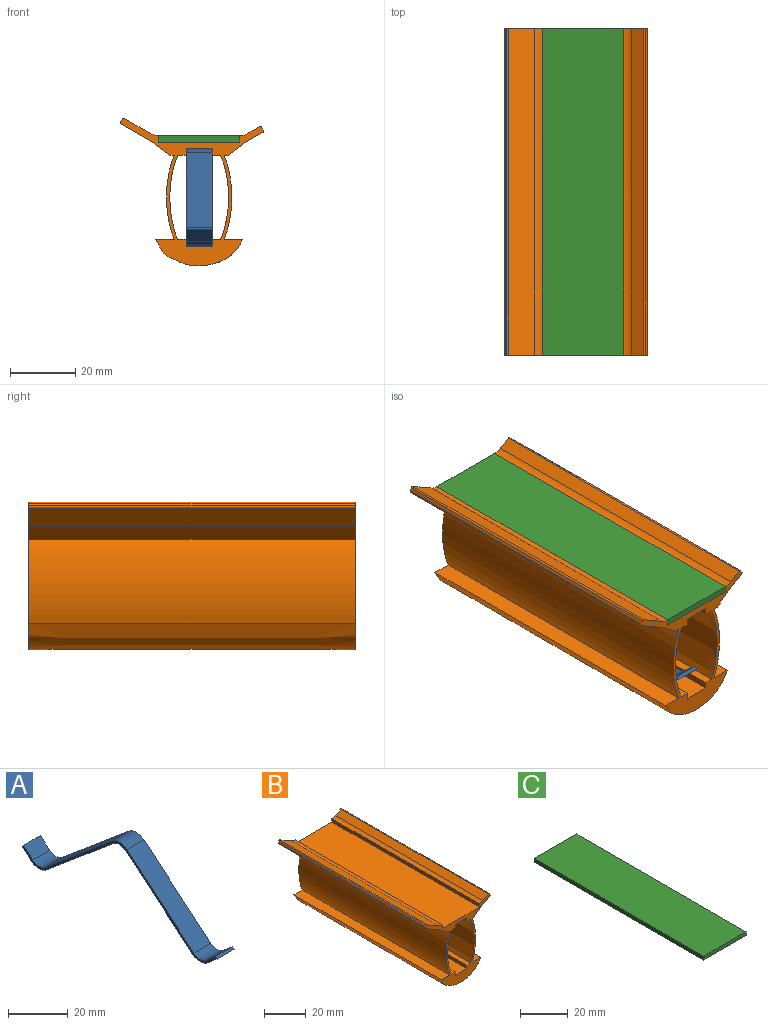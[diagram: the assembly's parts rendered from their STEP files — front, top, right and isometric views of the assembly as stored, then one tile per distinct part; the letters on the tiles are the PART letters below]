
ASSEMBLY  parts=3 mates=2
PART A: 18 faces, bbox 8x91.9x29.8 mm
  f0: plane 8x4.45mm, normal (0,0.64,0.77), area 46.4mm2, adj f1,f15,f16,f17
  f1: plane 8x0.77mm, normal (0,-0.77,0.64), area 8mm2, adj f0,f2,f16,f17
  f2: plane 8x4.45mm, normal (0,-0.64,-0.77), area 46.4mm2, adj f1,f3,f16,f17
  f3: cylinder r=5.5mm len=8mm, axis (-1,0,0), area 61.4mm2, adj f2,f4,f16,f17
  f4: plane 31.56x26.48mm, normal (0,0.64,-0.77), area 329.6mm2, adj f3,f5,f16,f17
  f5: cylinder r=4.5mm len=8mm, axis (-1,0,0), area 50.3mm2, adj f4,f6,f16,f17
  f6: plane 31.56x26.48mm, normal (0,-0.64,-0.77), area 329.6mm2, adj f5,f7,f16,f17
  f7: cylinder r=5.5mm len=8mm, axis (-1,0,0), area 61.4mm2, adj f6,f8,f16,f17
  f8: plane 8x4.45mm, normal (0,0.64,-0.77), area 46.4mm2, adj f7,f9,f16,f17
  f9: plane 8x0.77mm, normal (0,0.77,0.64), area 8mm2, adj f8,f10,f16,f17
  f10: plane 8x4.45mm, normal (0,-0.64,0.77), area 46.4mm2, adj f9,f11,f16,f17
  f11: cylinder r=4.5mm len=8mm, axis (-1,0,0), area 50.3mm2, adj f10,f12,f16,f17
  f12: plane 31.56x26.48mm, normal (0,0.64,0.77), area 329.6mm2, adj f11,f13,f16,f17
  f13: cylinder r=5.5mm len=8mm, axis (-1,0,0), area 61.4mm2, adj f12,f14,f16,f17
  f14: plane 31.56x26.48mm, normal (0,-0.64,0.77), area 329.6mm2, adj f13,f15,f16,f17
  f15: cylinder r=4.5mm len=8mm, axis (-1,0,0), area 50.3mm2, adj f0,f14,f16,f17
  f16: plane 91.95x29.82mm, normal (1,0,0), area 115mm2, adj f0,f1,f2,f3,f4,f5,f6,f7
  f17: plane 91.95x29.82mm, normal (-1,0,0), area 115mm2, adj f0,f1,f2,f3,f4,f5,f6,f7
PART B: 38 faces, bbox 43.9x100x45.3 mm
  f0: plane 45.29x43.89mm, normal (0,-1,0), area 313.5mm2, adj f1,f2,f3,f4,f5,f6,f7,f8
  f1: cylinder r=5mm len=100mm, axis (0,-1,0), area 252.8mm2, adj f0,f8,f10,f35
  f2: plane 100x2.55mm, normal (0,0,-1), area 254.7mm2, adj f0,f10,f15,f16
  f3: plane 100x1.36mm, normal (0,0,-1), area 136.3mm2, adj f0,f10,f20,f33
  f4: plane 100x9.58mm, normal (-0.5,0,-0.87), area 1106.1mm2, adj f0,f10,f31,f33
  f5: plane 100x5.23mm, normal (0.5,0,-0.87), area 603.6mm2, adj f0,f10,f28,f34
  f6: plane 100x0.87mm, normal (0.87,0,0.5), area 100mm2, adj f0,f10,f28,f29
  f7: plane 100x3.6mm, normal (-0.5,0,0.87), area 416mm2, adj f0,f10,f29,f32
  f8: plane 100x7.96mm, normal (0.5,0,0.87), area 918.6mm2, adj f0,f1,f10,f30
  f9: plane 100x0.87mm, normal (-0.87,0,0.5), area 100mm2, adj f0,f10,f30,f31
  f10: plane 45.29x43.89mm, normal (0,1,0), area 313.5mm2, adj f1,f2,f3,f4,f5,f6,f7,f8
  f11: plane 100x1.36mm, normal (0,0,-1), area 136.3mm2, adj f0,f10,f17,f34
  f12: plane 100x2.55mm, normal (0,0,-1), area 254.7mm2, adj f0,f10,f13,f19
  f13: plane 100x2mm, normal (1,0,0), area 200mm2, adj f0,f10,f12,f14
  f14: plane 100x8mm, normal (0,0,-1), area 800mm2, adj f0,f10,f13,f15
  f15: plane 100x2mm, normal (-1,0,0), area 200mm2, adj f0,f2,f10,f14
  f16: extruded ~100x25.82mm, area 2647.1mm2, adj f0,f2,f10,f18
  f17: extruded ~100x25.82mm, area 2642.1mm2, adj f0,f10,f11,f22
  f18: plane 100x2.55mm, normal (0,0,1), area 254.7mm2, adj f0,f10,f16,f27
  f19: extruded ~100x25.82mm, area 2647.1mm2, adj f0,f10,f12,f23
  f20: extruded ~100x25.82mm, area 2642.1mm2, adj f0,f3,f10,f21
  f21: plane 100x5.68mm, normal (0,0,1), area 567.6mm2, adj f0,f10,f20,f24
  f22: plane 100x5.63mm, normal (0,0,1), area 563.3mm2, adj f0,f10,f17,f24
  f23: plane 100x2.55mm, normal (0,0,1), area 254.7mm2, adj f0,f10,f19,f26
  f24: extruded ~100x26.58mm, area 3317.3mm2, adj f0,f10,f21,f22
  f25: plane 100x8mm, normal (0,0,1), area 800mm2, adj f0,f10,f26,f27
  f26: plane 100x2mm, normal (1,0,0), area 200mm2, adj f0,f10,f23,f25
  f27: plane 100x2mm, normal (-1,0,0), area 200mm2, adj f0,f10,f18,f25
  f28: cylinder r=0.5mm len=100mm, axis (0,1,0), area 78.5mm2, adj f0,f5,f6,f10
  f29: cylinder r=0.5mm len=100mm, axis (0,-1,0), area 78.5mm2, adj f0,f6,f7,f10
  f30: cylinder r=0.5mm len=100mm, axis (0,1,0), area 78.5mm2, adj f0,f8,f9,f10
  f31: cylinder r=0.5mm len=100mm, axis (0,-1,0), area 78.5mm2, adj f0,f4,f9,f10
  f32: cylinder r=5mm len=100mm, axis (0,-1,0), area 252.8mm2, adj f0,f7,f10,f36
  f33: plane 100x5.3mm, normal (-0.6,0,-0.8), area 664mm2, adj f0,f3,f4,f10
  f34: plane 100x5.27mm, normal (0.6,0,-0.8), area 661.8mm2, adj f0,f5,f10,f11
  f35: plane 100x2mm, normal (1,0,0), area 200mm2, adj f0,f1,f10,f37
  f36: plane 100x2mm, normal (-1,0,0), area 200mm2, adj f0,f10,f32,f37
  f37: plane 100x25mm, normal (0,0,1), area 2500mm2, adj f0,f10,f35,f36
PART C: 6 faces, bbox 25x100x2 mm
  f0: plane 100x2mm, normal (1,0,0), area 200mm2, adj f1,f3,f4,f5
  f1: plane 100x25mm, normal (0,0,1), area 2500mm2, adj f0,f2,f4,f5
  f2: plane 100x2mm, normal (-1,0,0), area 200mm2, adj f1,f3,f4,f5
  f3: plane 100x25mm, normal (0,0,-1), area 2500mm2, adj f0,f2,f4,f5
  f4: plane 25x2mm, normal (0,-1,0), area 50mm2, adj f0,f1,f2,f3
  f5: plane 25x2mm, normal (0,1,0), area 50mm2, adj f0,f1,f2,f3
PLACE A t=(56.5,-1.76,90.09)mm
PLACE B t=(4.26,-1.76,15.55)mm
PLACE C t=(56.49,-1.76,108.01)mm
MATE fastened A.f16 <-> B.f27  axis (1,0,0) through (60.5,-1.76,88.09)mm
MATE fastened C.f3 <-> B.f37  axis (0,0,-1) through (56.49,-1.76,107.01)mm
